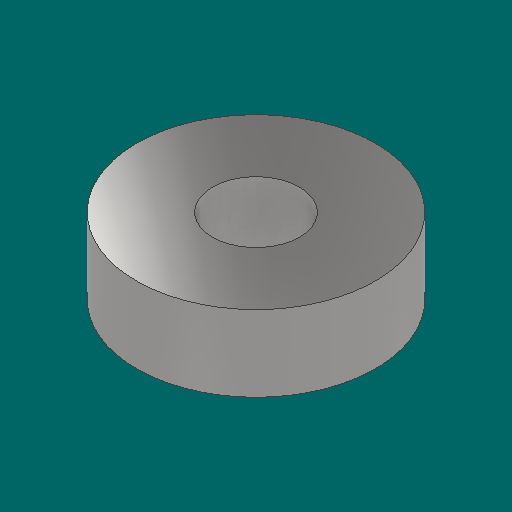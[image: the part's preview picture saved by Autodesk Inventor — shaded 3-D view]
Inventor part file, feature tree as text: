
AUTODESK INVENTOR PART (.ipt)
format: ipt  version: 2023.1 (Build 271208000, 208)  size: 107,520 bytes
history: native  units: in
note: dims shown in document units (in); Inventor stores cm internally (conversion verified against a paired STEP export)
features: extrude x1, sketch x1
ambient origin geometry x8: Origin, YZ Plane, XZ Plane, XY Plane, X Axis, Y Axis, Z Axis, Center Point
bodies: Solid1 (feature_tree)
feature tree (2):
  extrude  "Extrusion1"  Depth=0.2756in
  sketch  "Sketch1"  dims[d0=0.315in d1=0.8661in d2=0.2756in d3=0.0in]
